# Revit family: НЕВАТОМ_Клaпан КО (бабочка), Версия 2
name_source: partatom
category: Арматура воздуховодов
revit_build: Autodesk Revit 2017 (Build: 20170118_1100(x64)
units: mm (PartAtom-declared; Revit-internal decimal feet)

## family parameters
Всегда вертикально = Да
На основе рабочей плоскости = Нет
Общий = Нет
При загрузке вырезать с полостями = Нет
Размер круглого соединителя = Использовать диаметр
Тип детали = Вставляется

## types (6) — shared parameters
ADSK_Единица измерения = шт.
ADSK_Завод-изготовитель = НЕВАТОМ
ADSK_Количество = 1
ADSK_Материал наименование = Оцинкованная сталь
ADSK_Наименование = Обратный клапан круглого сечения(бабочка)
ADSK_Потеря давления воздуха = 0.0 Па
ADSK_Размер_Ширина = 80 мм
ADSK_Расход воздуха = 0.0 л/с
Nevatom_URL = https://t.me
Ключевая пометка = Вентиляция
Материал = Сталь оцинкованная

## per-type parameters (varying)
| type | ADSK_Марка | ADSK_Масса | ADSK_Размер_Высота | ADSK_Размер_Длина | D |
| КО 100 | КО 100 ("бабочка") | 0.21 | 100 мм | 100 мм | 100 мм |
| КО 315 | КО 315 ("бабочка") | 0.73 | 315 мм | 315 мм | 315 мм |
| КО 125 | КО 125 ("бабочка") | 0.27 | 125 мм | 125 мм | 125 мм |
| КО 160 | КО 160 ("бабочка") | 0.35 | 160 мм | 160 мм | 160 мм |
| КО 200 | КО 200 ("бабочка") | 0.44 | 200 мм | 200 мм | 200 мм |
| КО 250 | КО 250 ("бабочка") | 0.57 | 250 мм | 250 мм | 250 мм |
